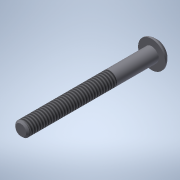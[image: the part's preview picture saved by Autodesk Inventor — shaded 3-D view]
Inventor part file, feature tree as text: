
AUTODESK INVENTOR PART (.ipt)
format: ipt  version: 2020 (Build 240168000, 168)  size: 129,024 bytes
history: native  units: in
note: dims shown in document units (in); Inventor stores cm internally (conversion verified against a paired STEP export)
features: sketch x3, extrude x2, revolve x1, chamfer x1, thread x1
ambient origin geometry x8: Origin, YZ Plane, XZ Plane, XY Plane, X Axis, Y Axis, Z Axis, Center Point
bodies: Solid1 (feature_tree)
feature tree (8):
  extrude  "Extrusion1"  Depth=1.5in TaperAngle=0.0deg
  revolve  "Revolution1"  [1 undecoded]
  extrude  "Extrusion2"  Depth=0.0938in
  chamfer  "Chamfer1"  Distance=0.0625in
  thread  "Thread1"  [1 undecoded]
  sketch  "Sketch1"  dims[d0=0.164in d1=1.5in d2=0.0in]
  sketch  "Sketch2"  dims[d3=0.087in d6=0.08in]
  sketch  "Sketch3"  dims[d7=90.0deg d8=0.0938in d9=0.0625in d10=0.0in d13=0.02in d14=0.125in d15=45.0deg d16=1.0in d17=0.0in d19=0.156in]
note: 2 required parameter values undecoded (feature->parameter linkage not recoverable at this tier; creation-order binding heuristic only, values carry confidence <= 0.55)